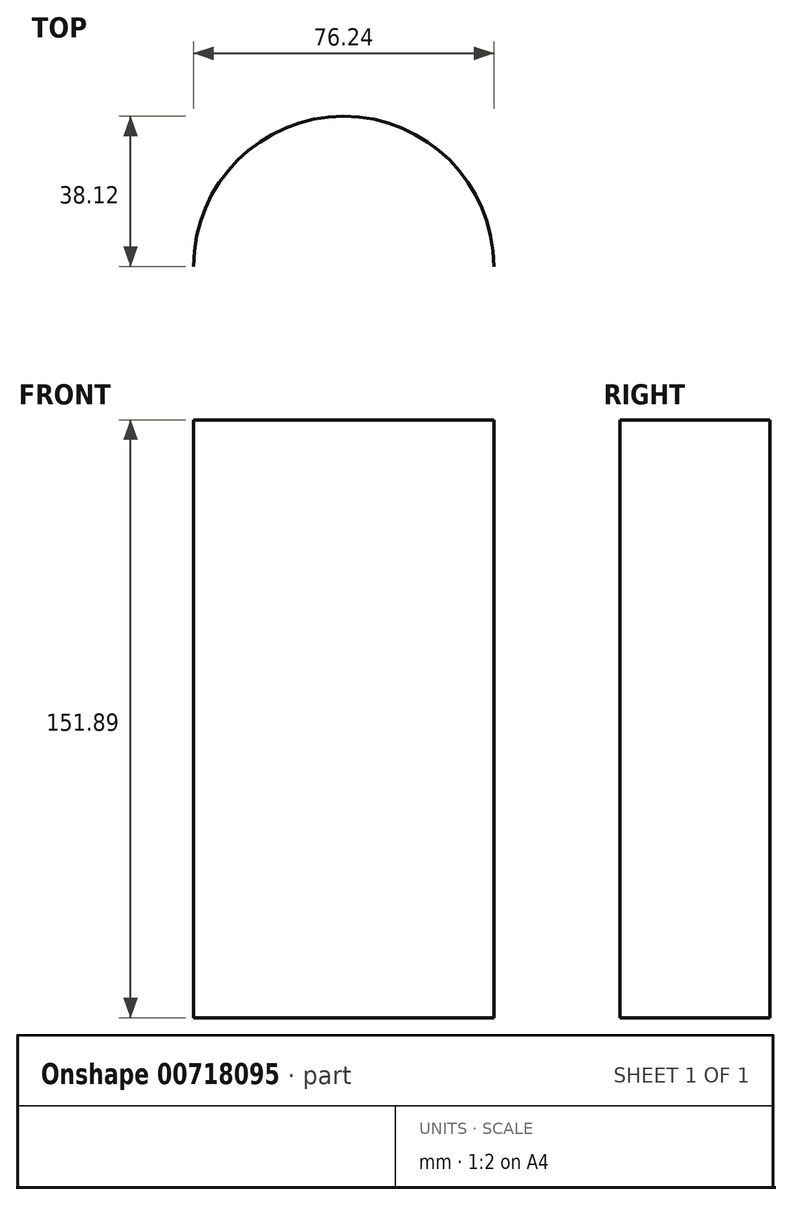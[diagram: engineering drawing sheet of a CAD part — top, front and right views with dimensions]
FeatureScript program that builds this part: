
annotation { "Feature Type Name" : "Feature", "Feature Type Description" : "" }
export const myFeature = defineFeature(function(context is Context, id is Id, definition is map)
    precondition{}
    {
        {
            var Q0;
            Q0=qCreatedBy(makeId("Top.planeOp"),FACE);
            var sketch = newSketch(context, id + "F0", { "sketchPlane" : qUnion([Q0])});
            skArc(sketch, "E0", {"start": v(0, 0) * mm, "mid": v(-38.12, 38.12) * mm, "end": v(-76.24, 0) * mm});
            skSolve(sketch);
        }
        {
            var Q0;
            Q0=sQuery(id+"F0.wireOp",EDGE,"E0");
            extrude(context, id + "F1", {"bodyType" : ToolBodyType.SURFACE, "surfaceEntities" : qUnion([Q0]), "depth" : 151.9 * mm, "offsetDistance" : 25.4 * mm});
        }
    });
